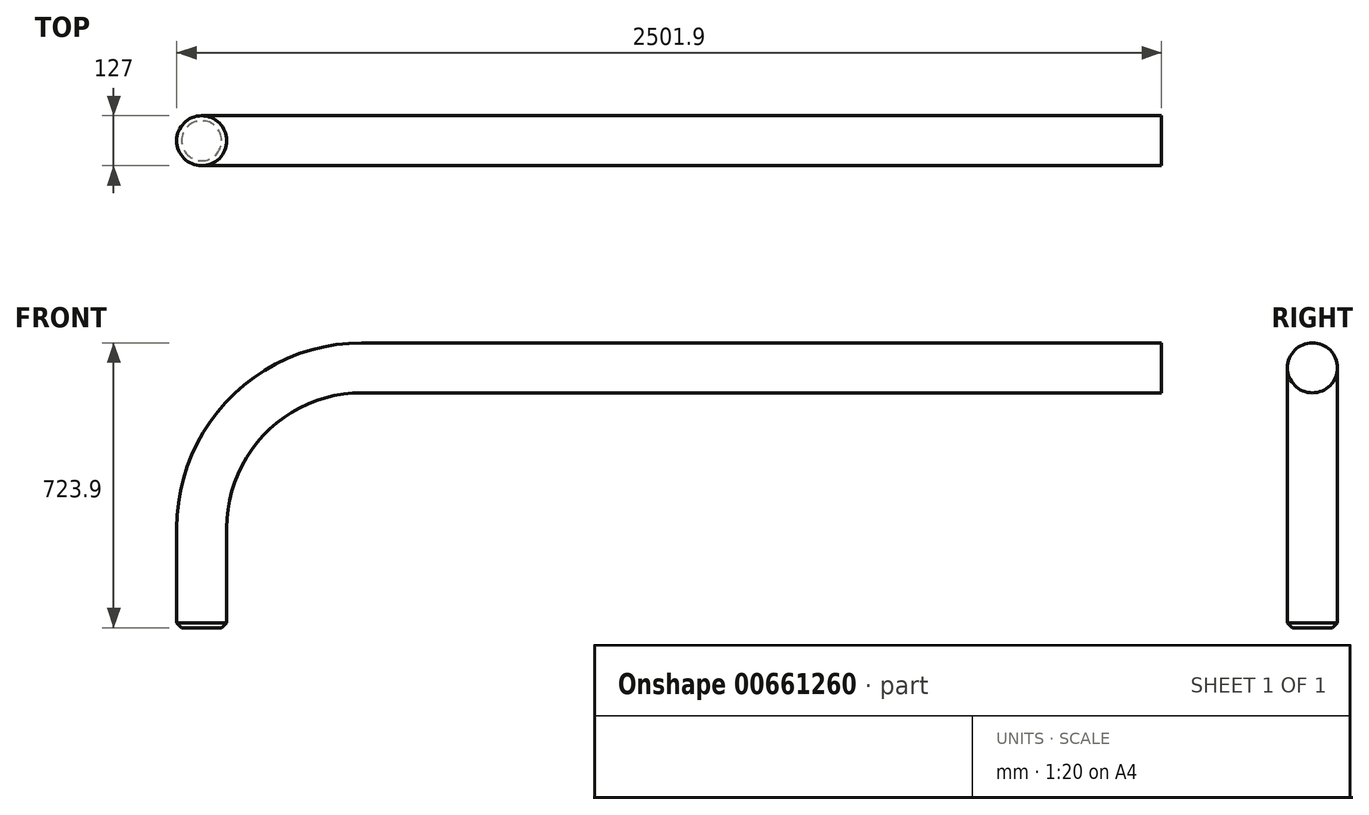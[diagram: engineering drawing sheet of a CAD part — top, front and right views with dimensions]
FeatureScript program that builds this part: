
annotation { "Feature Type Name" : "Feature", "Feature Type Description" : "" }
export const myFeature = defineFeature(function(context is Context, id is Id, definition is map)
    precondition{}
    {
        {
            var Q0;
            Q0=qCreatedBy(makeId("Front.planeOp"),FACE);
            var sketch = newSketch(context, id + "F0", { "sketchPlane" : qUnion([Q0])});
            skLineSegment(sketch, "E0", {"start": v(0, 375.18) * mm, "end": v(-2032, 375.18) * mm});
            skLineSegment(sketch, "E1", {"start": v(-2438.4, -31.22) * mm, "end": v(-2438.4, -285.22) * mm});
            skPoint(sketch, "E2.visualSharp", {"position": v(-2438.4, 375.18) * mm});
            skArc(sketch, "E2.filletArc", {"start": v(-2032, 375.18) * mm, "mid": v(-2319.37, 256.15) * mm, "end": v(-2438.4, -31.22) * mm});
            skSolve(sketch);
        }
        {
            var Q0;
            Q0=qCreatedBy(makeId("Right.planeOp"),FACE);
            var sketch = newSketch(context, id + "F1", { "sketchPlane" : qUnion([Q0])});
            skCircle(sketch, "E3", {"center": v(0, 375.18) * mm, "radius": 63.5 * mm});
            skSolve(sketch);
        }
        {
            var Q0;
            Q0=makeQuery(id+"F1.imprint","IMPRINT",FACE,{"disambiguationData":[TD([[makeQuery(id+"F1.imprint","IMPRINT",EDGE,{"derivedFrom":sQuery(id+"F1.wireOp",EDGE,"E3")}),1.0]])]});
            var Q1;
            Q1=sQuery(id+"F0.wireOp",EDGE,"E0");
            var Q2;
            Q2=sQuery(id+"F0.wireOp",EDGE,"E2.filletArc");
            var Q3;
            Q3=sQuery(id+"F0.wireOp",EDGE,"E1");
            sweep(context, id + "F2", {"profiles" : qUnion([Q0]), "path" : qUnion([Q1, Q2, Q3])});
        }
        {
            var Q0;
            Q0=makeQuery(id+"F2.opSweep","CAP_EDGE",EDGE,{"disambiguationData":[OSD([sQuery(id+"F0.wireOp",VERTEX,"E1.end"),sQuery(id+"F1.wireOp",EDGE,"E3")])],"isStart":false});
            chamfer(context, id + "F3", {"entities" : qUnion([Q0]), "chamferType" : ChamferType.OFFSET_ANGLE, "width" : 12.7 * mm, "oppositeDirection" : false, "angle" : 45 * degree, "tangentPropagation" : true});
        }
    });
